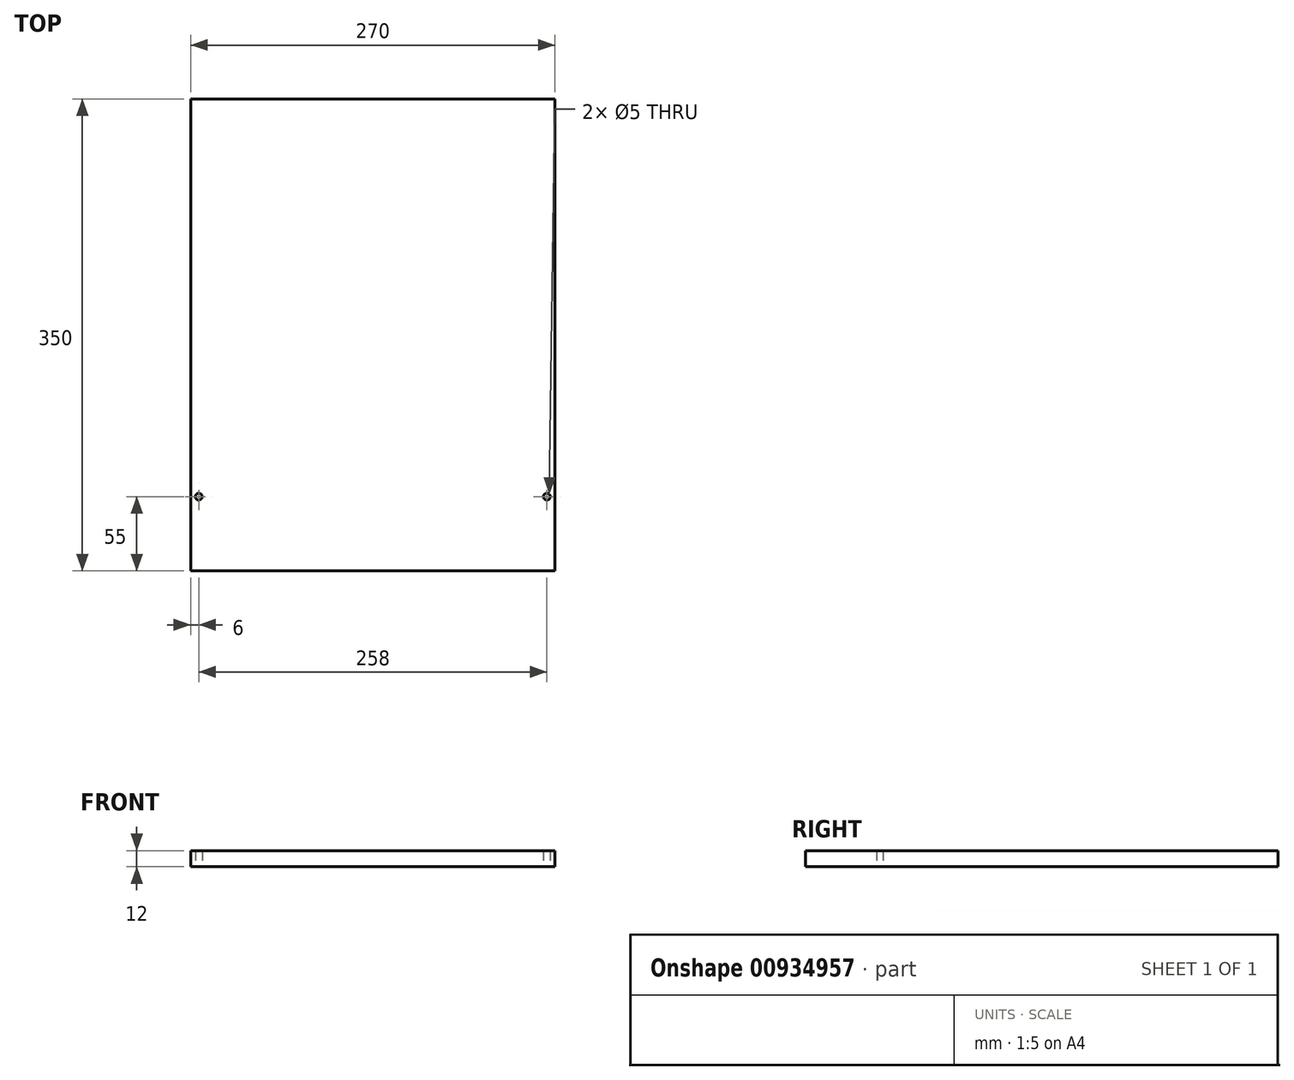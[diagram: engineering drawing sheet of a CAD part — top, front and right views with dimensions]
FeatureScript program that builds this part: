
annotation { "Feature Type Name" : "Feature", "Feature Type Description" : "" }
export const myFeature = defineFeature(function(context is Context, id is Id, definition is map)
    precondition{}
    {
        {
            var Q0;
            Q0=qCreatedBy(makeId("Top.planeOp"),FACE);
            var sketch = newSketch(context, id + "F0", { "sketchPlane" : qUnion([Q0])});
            skLineSegment(sketch, "E0.bottom", {"start": v(0, 0) * mm, "end": v(270, 0) * mm});
            skLineSegment(sketch, "E0.top", {"start": v(0, 350) * mm, "end": v(270, 350) * mm});
            skLineSegment(sketch, "E0.left", {"start": v(0, 0) * mm, "end": v(0, 350) * mm});
            skLineSegment(sketch, "E0.right", {"start": v(270, 0) * mm, "end": v(270, 350) * mm});
            skCircle(sketch, "E1", {"center": v(6, 55) * mm, "radius": 2.5 * mm});
            skPoint(sketch, "E2.orphan", {"position": v(0, 55) * mm});
            skPoint(sketch, "E3.start.orphan", {"position": v(135, 0) * mm});
            skCircle(sketch, "E4.MirrorC", {"center": v(264, 55) * mm, "radius": 2.5 * mm});
            skSolve(sketch);
        }
        {
            var Q0;
            Q0 = qSketchRegion(id + "F0", true);
            extrude(context, id + "F1", {"entities" : qUnion([Q0]), "depth" : 12 * mm, "offsetDistance" : 25 * mm});
        }
    });
